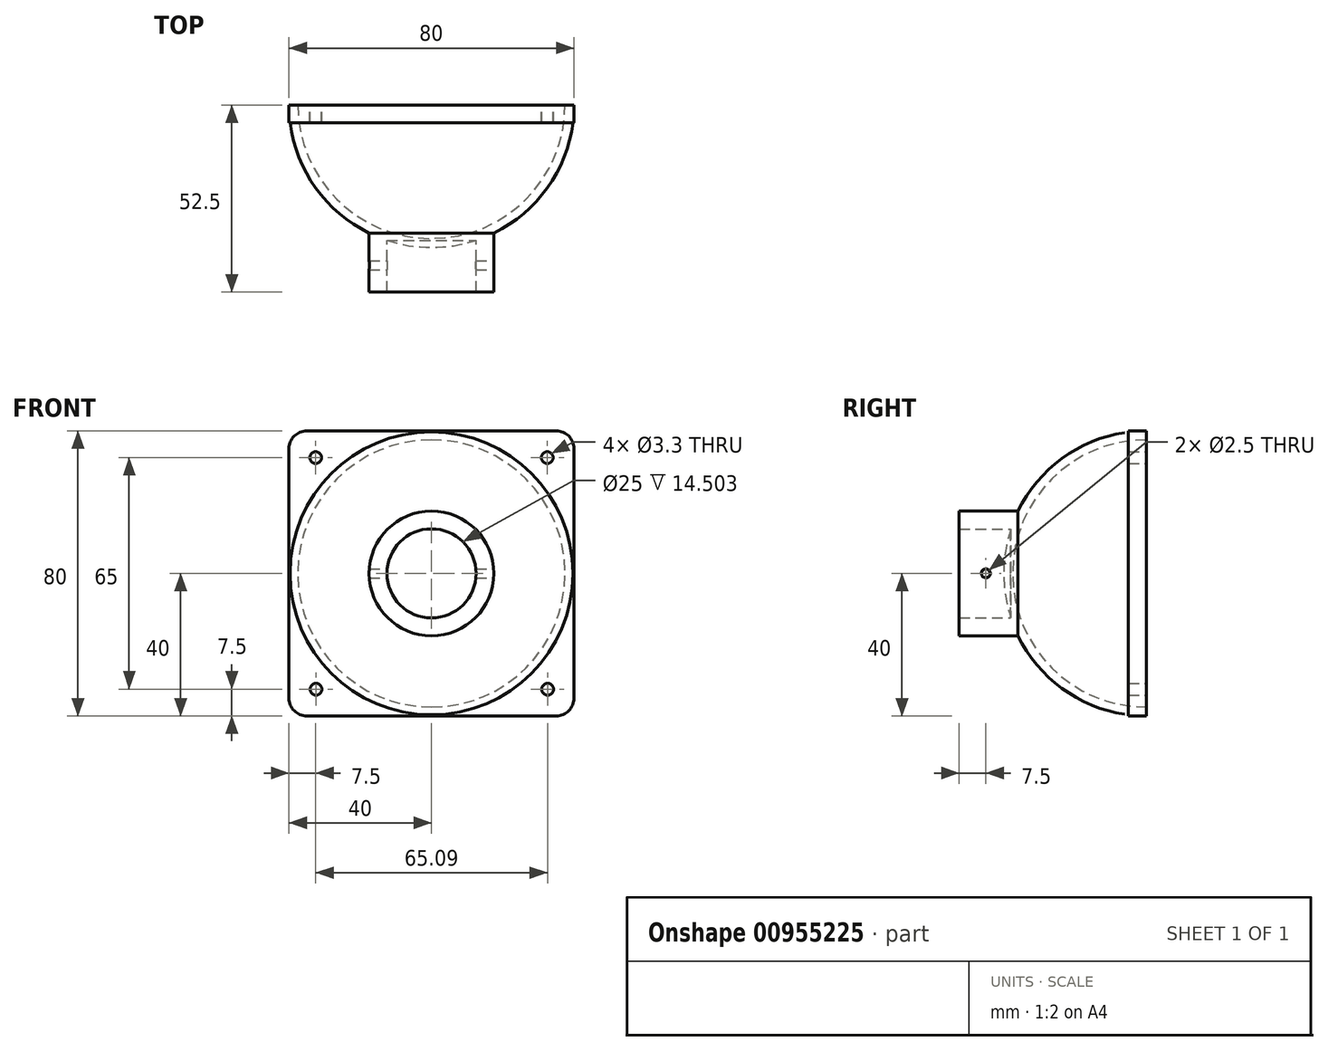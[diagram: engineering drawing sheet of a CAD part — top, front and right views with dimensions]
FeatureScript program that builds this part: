
annotation { "Feature Type Name" : "Feature", "Feature Type Description" : "" }
export const myFeature = defineFeature(function(context is Context, id is Id, definition is map)
    precondition{}
    {
        {
            var Q0;
            Q0=qCreatedBy(makeId("Front.planeOp"),FACE);
            var sketch = newSketch(context, id + "F0", { "sketchPlane" : qUnion([Q0])});
            skArc(sketch, "E0", {"start": v(0, -40) * mm, "mid": v(40, 0) * mm, "end": v(0, 40) * mm});
            skArc(sketch, "E1", {"start": v(0, -37.5) * mm, "mid": v(37.5, 0) * mm, "end": v(0, 37.5) * mm});
            skLineSegment(sketch, "E2", {"start": v(0, 40) * mm, "end": v(0, 37.5) * mm});
            skLineSegment(sketch, "E3.trimOffspring", {"start": v(0, -37.5) * mm, "end": v(0, -40) * mm});
            skSolve(sketch);
        }
        {
            var Q0;
            Q0=makeQuery(id+"F0.imprint","IMPRINT",FACE,{"disambiguationData":[TD([[makeQuery(id+"F0.imprint","IMPRINT",EDGE,{"derivedFrom":sQuery(id+"F0.wireOp",EDGE,"E0")}),1.0]])]});
            var Q1;
            Q1=sQuery(id+"F0.wireOp",EDGE,"E2");
            revolve(context, id + "F1", {"surfaceOperationType" : NewSurfaceOperationType.NEW, "entities" : qUnion([Q0]), "axis" : qUnion([Q1]), "revolveType" : RevolveType.ONE_DIRECTION, "angle" : 180 * degree});
        }
        {
            var Q0;
            Q0=makeQuery(id+"F1.opRevolve","CAP_FACE",FACE,{"disambiguationData":[OSD([sQuery(id+"F0.wireOp",EDGE,"E0"),sQuery(id+"F0.wireOp",EDGE,"E1"),sQuery(id+"F0.wireOp",EDGE,"E2"),sQuery(id+"F0.wireOp",EDGE,"E3.trimOffspring")])],"isStart":true});
            var sketch = newSketch(context, id + "F2", { "sketchPlane" : qUnion([Q0])});
            skLineSegment(sketch, "E4.bottom", {"start": v(-40, 40) * mm, "end": v(40, 40) * mm});
            skLineSegment(sketch, "E4.top", {"start": v(-40, -40) * mm, "end": v(40, -40) * mm});
            skLineSegment(sketch, "E4.left", {"start": v(-40, 40) * mm, "end": v(-40, -40) * mm});
            skLineSegment(sketch, "E4.right", {"start": v(40, 40) * mm, "end": v(40, -40) * mm});
            skPoint(sketch, "E4.middle", {"position": v(0, 0) * mm});
            skCircle(sketch, "E5", {"center": v(0, 0) * mm, "radius": 37.5 * mm});
            skSolve(sketch);
        }
        {
            var Q0;
            Q0 = qSketchRegion(id + "F2", true);
            extrude(context, id + "F3", {"entities" : qUnion([Q0]), "operationType" : NewBodyOperationType.ADD, "oppositeDirection" : true, "depth" : 5 * mm, "offsetDistance" : 25 * mm});
        }
        {
            var Q0;
            Q0=qCreatedBy(makeId("Front.planeOp"),FACE);
            var sketch = newSketch(context, id + "F4", { "sketchPlane" : qUnion([Q0])});
            skPoint(sketch, "E6", {"position": v(-32.5, 32.5) * mm});
            skPoint(sketch, "E7.0.1.0", {"position": v(-32.41, -32.5) * mm});
            skPoint(sketch, "E7.1.0.0", {"position": v(32.5, 32.5) * mm});
            skPoint(sketch, "E7.1.1.0", {"position": v(32.59, -32.5) * mm});
            skLineSegment(sketch, "E7.direction1", {"start": v(-32.5, 32.5) * mm, "end": v(32.5, 32.5) * mm, "construction": true});
            skLineSegment(sketch, "E7.direction2", {"start": v(-32.5, 32.5) * mm, "end": v(-32.41, -32.5) * mm, "construction": true});
            skSolve(sketch);
        }
        {
            var Q0;
            Q0=sQuery(id+"F4.wireOp",VERTEX,"E6");
            var Q1;
            Q1=sQuery(id+"F4.wireOp",VERTEX,"E7.1.0.0");
            var Q2;
            Q2=sQuery(id+"F4.wireOp",VERTEX,"E7.0.1.0");
            var Q3;
            Q3=sQuery(id+"F4.wireOp",VERTEX,"E7.1.1.0");
            var Q4;
            Q4=makeQuery(id+"F1.opRevolve","SWEPT_BODY",BODY,{"disambiguationData":[OSD([sQuery(id+"F0.wireOp",EDGE,"E0"),sQuery(id+"F0.wireOp",EDGE,"E1"),sQuery(id+"F0.wireOp",EDGE,"E2"),sQuery(id+"F0.wireOp",EDGE,"E3.trimOffspring")])]});
            hole(context, id + "F5", {"style" : HoleStyle.SIMPLE, "endStyle" : HoleEndStyle.THROUGH, "oppositeDirection" : true, "standardTappedOrClearance" : lookupTablePath({ "standard" : "ISO", "engagement" : "75%", "pitch" : "0.7 mm", "size" : "M4", "type" : "Tapped" }), "standardBlindInLast" : lookupTablePath({ "standard" : "ISO", "fit" : "Normal", "engagement" : "75%", "pitch" : "0.7 mm", "size" : "M4", "type" : "Clearance & tapped" }), "holeDiameter" : 3.3 * mm, "majorDiameter" : 4 * mm, "showTappedDepth" : true, "isTappedThrough" : true, "tappedDepth" : 12 * mm, "tapClearance" : 3, "locations" : qUnion([Q0, Q1, Q2, Q3]), "scope" : qUnion([Q4])});
        }
        {
            var Q0;
            Q0=makeQuery(id+"F3.opExtrude","CAP_FACE",FACE,{"disambiguationData":[OSD([sQuery(id+"F2.wireOp",EDGE,"E4.bottom"),sQuery(id+"F2.wireOp",EDGE,"E4.top"),sQuery(id+"F2.wireOp",EDGE,"E4.left"),sQuery(id+"F2.wireOp",EDGE,"E4.right"),sQuery(id+"F2.wireOp",EDGE,"E5")])],"isStart":false});
            cPlane(context, id + "F6", {"entities" : qUnion([Q0]), "cplaneType" : CPlaneType.OFFSET, "offset" : 32.5 * mm, "width" : 150 * mm, "height" : 150 * mm});
        }
        {
            var Q0;
            Q0=qCreatedBy(id+"F6.planeOp",FACE);
            var sketch = newSketch(context, id + "F7", { "sketchPlane" : qUnion([Q0])});
            skCircle(sketch, "E8", {"center": v(0, 0) * mm, "radius": 12.5 * mm});
            skCircle(sketch, "E9", {"center": v(0, 0) * mm, "radius": 17.5 * mm});
            skSolve(sketch);
        }
        {
            var Q0;
            Q0 = qSketchRegion(id + "F7", true);
            extrude(context, id + "F8", {"entities" : qUnion([Q0]), "operationType" : NewBodyOperationType.ADD, "depth" : 15 * mm, "offsetDistance" : 25 * mm});
        }
        {
            var Q0;
            Q0 = qSketchRegion(id + "F7", true);
            extrude(context, id + "F9", {"entities" : qUnion([Q0]), "operationType" : NewBodyOperationType.ADD, "endBound" : BoundingType.UP_TO_NEXT, "oppositeDirection" : true, "depth" : 25 * mm, "offsetDistance" : 25 * mm});
        }
        {
            var Q0;
            Q0=qCreatedBy(makeId("Right.planeOp"),FACE);
            cPlane(context, id + "F10", {"entities" : qUnion([Q0]), "cplaneType" : CPlaneType.OFFSET, "offset" : 35 * mm, "width" : 150 * mm, "height" : 150 * mm});
        }
        {
            var Q0;
            Q0=qCreatedBy(id+"F10.planeOp",FACE);
            var sketch = newSketch(context, id + "F11", { "sketchPlane" : qUnion([Q0])});
            skPoint(sketch, "E10", {"position": v(-45, 0) * mm});
            skSolve(sketch);
        }
        {
            var Q0;
            Q0=sQuery(id+"F11.wireOp",VERTEX,"E10");
            var Q1;
            Q1=makeQuery(id+"F1.opRevolve","SWEPT_BODY",BODY,{"disambiguationData":[OSD([sQuery(id+"F0.wireOp",EDGE,"E0"),sQuery(id+"F0.wireOp",EDGE,"E1"),sQuery(id+"F0.wireOp",EDGE,"E2"),sQuery(id+"F0.wireOp",EDGE,"E3.trimOffspring")])]});
            hole(context, id + "F12", {"style" : HoleStyle.SIMPLE, "endStyle" : HoleEndStyle.THROUGH, "standardTappedOrClearance" : lookupTablePath({ "standard" : "ISO", "engagement" : "75%", "pitch" : "0.5 mm", "size" : "M3", "type" : "Tapped" }), "standardBlindInLast" : lookupTablePath({ "standard" : "ISO", "fit" : "Normal", "engagement" : "75%", "pitch" : "0.5 mm", "size" : "M3", "type" : "Clearance & tapped" }), "holeDiameter" : 2.5 * mm, "majorDiameter" : 3 * mm, "showTappedDepth" : true, "isTappedThrough" : true, "tappedDepth" : 12 * mm, "tapClearance" : 3, "locations" : qUnion([Q0]), "scope" : qUnion([Q1])});
        }
        {
            var Q0;
            Q0=makeQuery(id+"F3.opExtrude","SWEPT_EDGE",EDGE,{"disambiguationData":[OSD([sQuery(id+"F2.wireOp",EDGE,"E4.bottom"),sQuery(id+"F2.wireOp",EDGE,"E4.right")])]});
            var Q1;
            Q1=makeQuery(id+"F3.opExtrude","SWEPT_EDGE",EDGE,{"disambiguationData":[OSD([sQuery(id+"F2.wireOp",EDGE,"E4.bottom"),sQuery(id+"F2.wireOp",EDGE,"E4.left")])]});
            var Q2;
            Q2=makeQuery(id+"F3.opExtrude","SWEPT_EDGE",EDGE,{"disambiguationData":[OSD([sQuery(id+"F2.wireOp",EDGE,"E4.top"),sQuery(id+"F2.wireOp",EDGE,"E4.right")])]});
            var Q3;
            Q3=makeQuery(id+"F3.opExtrude","SWEPT_EDGE",EDGE,{"disambiguationData":[OSD([sQuery(id+"F2.wireOp",EDGE,"E4.top"),sQuery(id+"F2.wireOp",EDGE,"E4.left")])]});
            fillet(context, id + "F13", {"entities" : qUnion([Q0, Q1, Q2, Q3]), "radius" : 5 * mm, "tangentPropagation" : true, "allowEdgeOverflow" : false});
        }
    });
